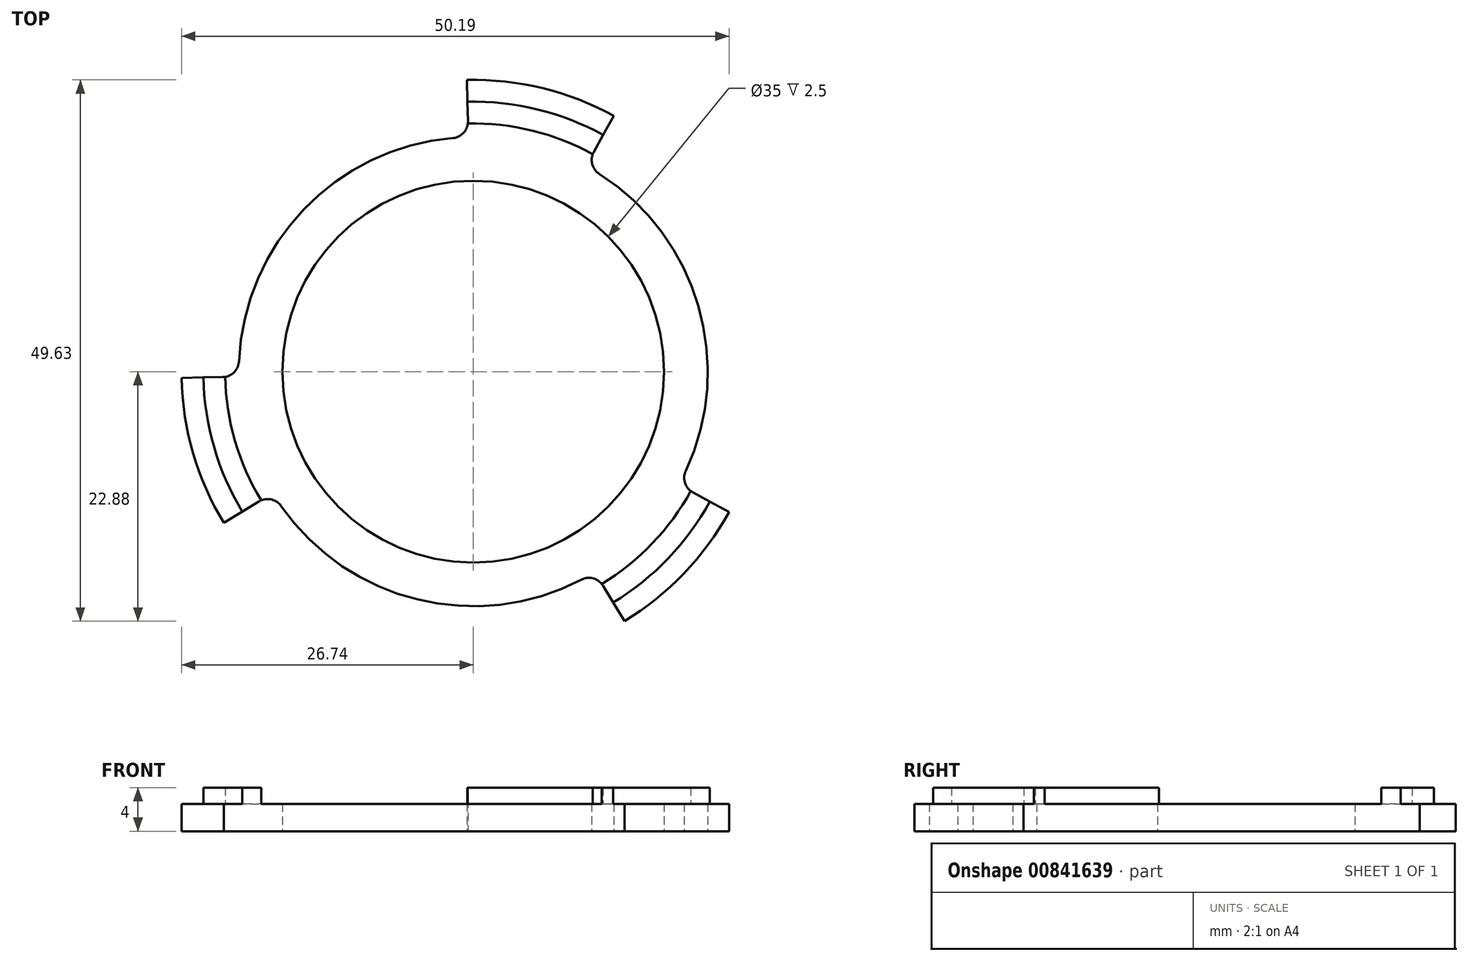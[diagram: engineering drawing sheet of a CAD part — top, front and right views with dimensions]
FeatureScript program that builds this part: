
annotation { "Feature Type Name" : "Feature", "Feature Type Description" : "" }
export const myFeature = defineFeature(function(context is Context, id is Id, definition is map)
    precondition{}
    {
        {
            var Q0;
            Q0=qCreatedBy(makeId("Top.planeOp"),FACE);
            var sketch = newSketch(context, id + "F0", { "sketchPlane" : qUnion([Q0])});
            skCircle(sketch, "E0", {"center": v(0, 0) * mm, "radius": 26.75 * mm});
            skCircle(sketch, "E1", {"center": v(0, 0) * mm, "radius": 24.75 * mm});
            skCircle(sketch, "E2", {"center": v(0, 0) * mm, "radius": 17.5 * mm});
            skCircle(sketch, "E3", {"center": v(0, 0) * mm, "radius": 21.5 * mm});
            skLineSegment(sketch, "E4", {"start": v(0, 0) * mm, "end": v(12.88, 23.45) * mm});
            skLineSegment(sketch, "E5", {"start": v(0, 0) * mm, "end": v(13.87, -22.88) * mm});
            skLineSegment(sketch, "E6", {"start": v(0, 0) * mm, "end": v(-26.74, -0.57) * mm});
            skLineSegment(sketch, "E7", {"start": v(0, 0) * mm, "end": v(-22.88, -13.87) * mm});
            skLineSegment(sketch, "E8", {"start": v(0, 0) * mm, "end": v(-0.57, 26.74) * mm});
            skLineSegment(sketch, "E9", {"start": v(0, 0) * mm, "end": v(23.45, -12.88) * mm});
            skCircle(sketch, "E10", {"center": v(0, 0) * mm, "radius": 22.75 * mm});
            skSolve(sketch);
        }
        {
            var Q0;
            {var subQ0=sQuery(id+"F0.wireOp",EDGE,"E8");var subQ1=sQuery(id+"F0.wireOp",EDGE,"E1");var subQ2=makeQuery(id+"F0.imprint","INTERSECT",VERTEX,{"derivedFrom":[subQ1,subQ0]});Q0=makeQuery(id+"F0.imprint","IMPRINT",FACE,{"disambiguationData":[TD([[makeQuery(id+"F0.imprint","IMPRINT",EDGE,{"disambiguationData":[TD([[subQ2,1.0]])],"derivedFrom":subQ1}),1.0]])]});}
            var Q1;
            {var subQ0=sQuery(id+"F0.wireOp",EDGE,"E6");var subQ1=sQuery(id+"F0.wireOp",EDGE,"E1");var subQ2=makeQuery(id+"F0.imprint","INTERSECT",VERTEX,{"derivedFrom":[subQ1,subQ0]});Q1=makeQuery(id+"F0.imprint","IMPRINT",FACE,{"disambiguationData":[TD([[makeQuery(id+"F0.imprint","IMPRINT",EDGE,{"disambiguationData":[TD([[subQ2,-1.0]])],"derivedFrom":subQ1}),1.0]])]});}
            var Q2;
            {var subQ0=sQuery(id+"F0.wireOp",EDGE,"E5");var subQ1=sQuery(id+"F0.wireOp",EDGE,"E1");var subQ2=makeQuery(id+"F0.imprint","INTERSECT",VERTEX,{"derivedFrom":[subQ1,subQ0]});Q2=makeQuery(id+"F0.imprint","IMPRINT",FACE,{"disambiguationData":[TD([[makeQuery(id+"F0.imprint","IMPRINT",EDGE,{"disambiguationData":[TD([[subQ2,-1.0]])],"derivedFrom":subQ1}),1.0]])]});}
            extrude(context, id + "F1", {"entities" : qUnion([Q0, Q1, Q2]), "depth" : 4 * mm, "offsetDistance" : 25 * mm});
        }
        {
            var Q0;
            {var subQ0=sQuery(id+"F0.wireOp",EDGE,"E4");var subQ1=sQuery(id+"F0.wireOp",EDGE,"E0");var subQ2=makeQuery(id+"F0.imprint","INTERSECT",VERTEX,{"derivedFrom":[subQ1,subQ0]});Q0=makeQuery(id+"F0.imprint","IMPRINT",FACE,{"disambiguationData":[TD([[makeQuery(id+"F0.imprint","IMPRINT",EDGE,{"disambiguationData":[TD([[subQ2,-1.0]])],"derivedFrom":subQ1}),1.0]])]});}
            var Q1;
            {var subQ0=sQuery(id+"F0.wireOp",EDGE,"E6");var subQ1=sQuery(id+"F0.wireOp",EDGE,"E0");var subQ2=makeQuery(id+"F0.imprint","INTERSECT",VERTEX,{"derivedFrom":[subQ1,subQ0]});Q1=makeQuery(id+"F0.imprint","IMPRINT",FACE,{"disambiguationData":[TD([[makeQuery(id+"F0.imprint","IMPRINT",EDGE,{"disambiguationData":[TD([[subQ2,-1.0]])],"derivedFrom":subQ1}),1.0]])]});}
            var Q2;
            {var subQ0=sQuery(id+"F0.wireOp",EDGE,"E5");var subQ1=sQuery(id+"F0.wireOp",EDGE,"E0");var subQ2=makeQuery(id+"F0.imprint","INTERSECT",VERTEX,{"derivedFrom":[subQ1,subQ0]});Q2=makeQuery(id+"F0.imprint","IMPRINT",FACE,{"disambiguationData":[TD([[makeQuery(id+"F0.imprint","IMPRINT",EDGE,{"disambiguationData":[TD([[subQ2,-1.0]])],"derivedFrom":subQ1}),1.0]])]});}
            var Q3;
            {var subQ0=sQuery(id+"F0.wireOp",EDGE,"E8");var subQ1=sQuery(id+"F0.wireOp",EDGE,"E2");var subQ2=makeQuery(id+"F0.imprint","INTERSECT",VERTEX,{"derivedFrom":[subQ1,subQ0]});Q3=makeQuery(id+"F0.imprint","IMPRINT",FACE,{"disambiguationData":[TD([[makeQuery(id+"F0.imprint","IMPRINT",EDGE,{"disambiguationData":[TD([[subQ2,1.0]])],"derivedFrom":subQ1}),-1.0]])]});}
            var Q4;
            {var subQ0=sQuery(id+"F0.wireOp",EDGE,"E8");var subQ1=sQuery(id+"F0.wireOp",EDGE,"E2");var subQ2=makeQuery(id+"F0.imprint","INTERSECT",VERTEX,{"derivedFrom":[subQ1,subQ0]});Q4=makeQuery(id+"F0.imprint","IMPRINT",FACE,{"disambiguationData":[TD([[makeQuery(id+"F0.imprint","IMPRINT",EDGE,{"disambiguationData":[TD([[subQ2,-1.0]])],"derivedFrom":subQ1}),-1.0]])]});}
            var Q5;
            {var subQ0=sQuery(id+"F0.wireOp",EDGE,"E6");var subQ1=sQuery(id+"F0.wireOp",EDGE,"E2");var subQ2=makeQuery(id+"F0.imprint","INTERSECT",VERTEX,{"derivedFrom":[subQ1,subQ0]});Q5=makeQuery(id+"F0.imprint","IMPRINT",FACE,{"disambiguationData":[TD([[makeQuery(id+"F0.imprint","IMPRINT",EDGE,{"disambiguationData":[TD([[subQ2,-1.0]])],"derivedFrom":subQ1}),-1.0]])]});}
            var Q6;
            {var subQ0=sQuery(id+"F0.wireOp",EDGE,"E7");var subQ1=sQuery(id+"F0.wireOp",EDGE,"E2");var subQ2=makeQuery(id+"F0.imprint","INTERSECT",VERTEX,{"derivedFrom":[subQ1,subQ0]});Q6=makeQuery(id+"F0.imprint","IMPRINT",FACE,{"disambiguationData":[TD([[makeQuery(id+"F0.imprint","IMPRINT",EDGE,{"disambiguationData":[TD([[subQ2,-1.0]])],"derivedFrom":subQ1}),-1.0]])]});}
            var Q7;
            {var subQ0=sQuery(id+"F0.wireOp",EDGE,"E5");var subQ1=sQuery(id+"F0.wireOp",EDGE,"E2");var subQ2=makeQuery(id+"F0.imprint","INTERSECT",VERTEX,{"derivedFrom":[subQ1,subQ0]});Q7=makeQuery(id+"F0.imprint","IMPRINT",FACE,{"disambiguationData":[TD([[makeQuery(id+"F0.imprint","IMPRINT",EDGE,{"disambiguationData":[TD([[subQ2,-1.0]])],"derivedFrom":subQ1}),-1.0]])]});}
            var Q8;
            {var subQ0=sQuery(id+"F0.wireOp",EDGE,"E4");var subQ1=sQuery(id+"F0.wireOp",EDGE,"E2");var subQ2=makeQuery(id+"F0.imprint","INTERSECT",VERTEX,{"derivedFrom":[subQ1,subQ0]});Q8=makeQuery(id+"F0.imprint","IMPRINT",FACE,{"disambiguationData":[TD([[makeQuery(id+"F0.imprint","IMPRINT",EDGE,{"disambiguationData":[TD([[subQ2,1.0]])],"derivedFrom":subQ1}),-1.0]])]});}
            var Q9;
            {var subQ0=sQuery(id+"F0.wireOp",EDGE,"E6");var subQ1=sQuery(id+"F0.wireOp",EDGE,"E3");var subQ2=makeQuery(id+"F0.imprint","INTERSECT",VERTEX,{"derivedFrom":[subQ1,subQ0]});Q9=makeQuery(id+"F0.imprint","IMPRINT",FACE,{"disambiguationData":[TD([[makeQuery(id+"F0.imprint","IMPRINT",EDGE,{"disambiguationData":[TD([[subQ2,-1.0]])],"derivedFrom":subQ1}),-1.0]])]});}
            var Q10;
            {var subQ0=sQuery(id+"F0.wireOp",EDGE,"E5");var subQ1=sQuery(id+"F0.wireOp",EDGE,"E3");var subQ2=makeQuery(id+"F0.imprint","INTERSECT",VERTEX,{"derivedFrom":[subQ1,subQ0]});Q10=makeQuery(id+"F0.imprint","IMPRINT",FACE,{"disambiguationData":[TD([[makeQuery(id+"F0.imprint","IMPRINT",EDGE,{"disambiguationData":[TD([[subQ2,-1.0]])],"derivedFrom":subQ1}),-1.0]])]});}
            var Q11;
            {var subQ0=sQuery(id+"F0.wireOp",EDGE,"E8");var subQ1=sQuery(id+"F0.wireOp",EDGE,"E3");var subQ2=makeQuery(id+"F0.imprint","INTERSECT",VERTEX,{"derivedFrom":[subQ1,subQ0]});Q11=makeQuery(id+"F0.imprint","IMPRINT",FACE,{"disambiguationData":[TD([[makeQuery(id+"F0.imprint","IMPRINT",EDGE,{"disambiguationData":[TD([[subQ2,1.0]])],"derivedFrom":subQ1}),-1.0]])]});}
            extrude(context, id + "F2", {"entities" : qUnion([Q0, Q1, Q2, Q3, Q4, Q5, Q6, Q7, Q8, Q9, Q10, Q11]), "operationType" : NewBodyOperationType.ADD, "depth" : 2.5 * mm, "offsetDistance" : 25 * mm});
        }
        {
            var Q0;
            Q0=makeQuery(id+"F2.opExtrude","SWEPT_EDGE",EDGE,{"disambiguationData":[OSD([sQuery(id+"F0.wireOp",EDGE,"E3"),sQuery(id+"F0.wireOp",EDGE,"E7")])]});
            var Q1;
            Q1=makeQuery(id+"F2.opExtrude","SWEPT_EDGE",EDGE,{"disambiguationData":[OSD([sQuery(id+"F0.wireOp",EDGE,"E3"),sQuery(id+"F0.wireOp",EDGE,"E5")])]});
            var Q2;
            Q2=makeQuery(id+"F2.opExtrude","SWEPT_EDGE",EDGE,{"disambiguationData":[OSD([sQuery(id+"F0.wireOp",EDGE,"E3"),sQuery(id+"F0.wireOp",EDGE,"E9")])]});
            var Q3;
            Q3=makeQuery(id+"F2.opExtrude","SWEPT_EDGE",EDGE,{"disambiguationData":[OSD([sQuery(id+"F0.wireOp",EDGE,"E3"),sQuery(id+"F0.wireOp",EDGE,"E4")])]});
            var Q4;
            Q4=makeQuery(id+"F2.opExtrude","SWEPT_EDGE",EDGE,{"disambiguationData":[OSD([sQuery(id+"F0.wireOp",EDGE,"E3"),sQuery(id+"F0.wireOp",EDGE,"E8")])]});
            var Q5;
            Q5=makeQuery(id+"F2.opExtrude","SWEPT_EDGE",EDGE,{"disambiguationData":[OSD([sQuery(id+"F0.wireOp",EDGE,"E3"),sQuery(id+"F0.wireOp",EDGE,"E6")])]});
            fillet(context, id + "F3", {"entities" : qUnion([Q0, Q1, Q2, Q3, Q4, Q5]), "radius" : 1.5 * mm, "tangentPropagation" : true, "allowEdgeOverflow" : false});
        }
    });
